# Revit family: ащк гзвфеу_36773CHN_туц
name_source: partatom
category: Plumbing Fixtures
revit_build: Autodesk Revit 2018 (Build: 20170223_1515(x64)
units: mm (PartAtom-declared; Revit-internal decimal feet)

## family parameters
Always vertical = No
Cut with Voids When Loaded = No
OmniClass Number = 23.31.17.00
OmniClass Title = Showers
Part Type = Normal
Room Calculation Point = No
Round Connector Dimension = Use Diameter
Shared = No
Work Plane-Based = Yes

## types (4) — shared parameters
Always visible = Yes
BIMobject category = Showers
Default Elevation = 1219.2 mm  [stored 4 ft]
Description = AXOR ShowerSelect Valve for concealed installation softsquare for 3 functions
Design country = Germany
EAN code = 4059625428573
Edition number = 1
GTIN code = https://4059625428573
IFC Classification = Sanitary Terminal
Manufacturer = AXOR
Manufacturer country = Germany
Manufacturer name = AXOR
Material 2 = AXOR - Plastic - Dark Gray
Model = 36773CHN
OmniClass Code = 23-31 17 00
OmniClass Description = Showers
Product Guid = 805d5ee2-d149-4050-965a-b15bdb5813ea
Product SKU = 36773CHN
Product data url = https://bimobject.com
Product family = AXOR ShowerSelect
Product group = Shower thermostat
Product name = 36773CHN AXOR ShowerSelect Valve for concealed installation softsquare for 3 functions
QR code = https://bimobject.com
URL = https://www.axor-design.com
Weight Net (Kg) = 1.9

## per-type parameters (varying)
| type | Material 1 |
| 347 Brushed Black Chrome | AXOR - Metal - 347 Brushed Black Chrome |
| 997 Polished Gold Optic | AXOR - Metal - 997 Polished Gold Optic |
| 677 Matt Black | AXOR - Metal - 677 Matt Black |
| 007 Chrome | AXOR - Metal - 007 Chrome |

note: [stored X ft] marks values corroborated as IEEE doubles in the binary element streams (Revit-internal decimal feet)

## geometry (parser evidence)
native form markers: Sweep x3
no freeform markers — native parametric forms only
